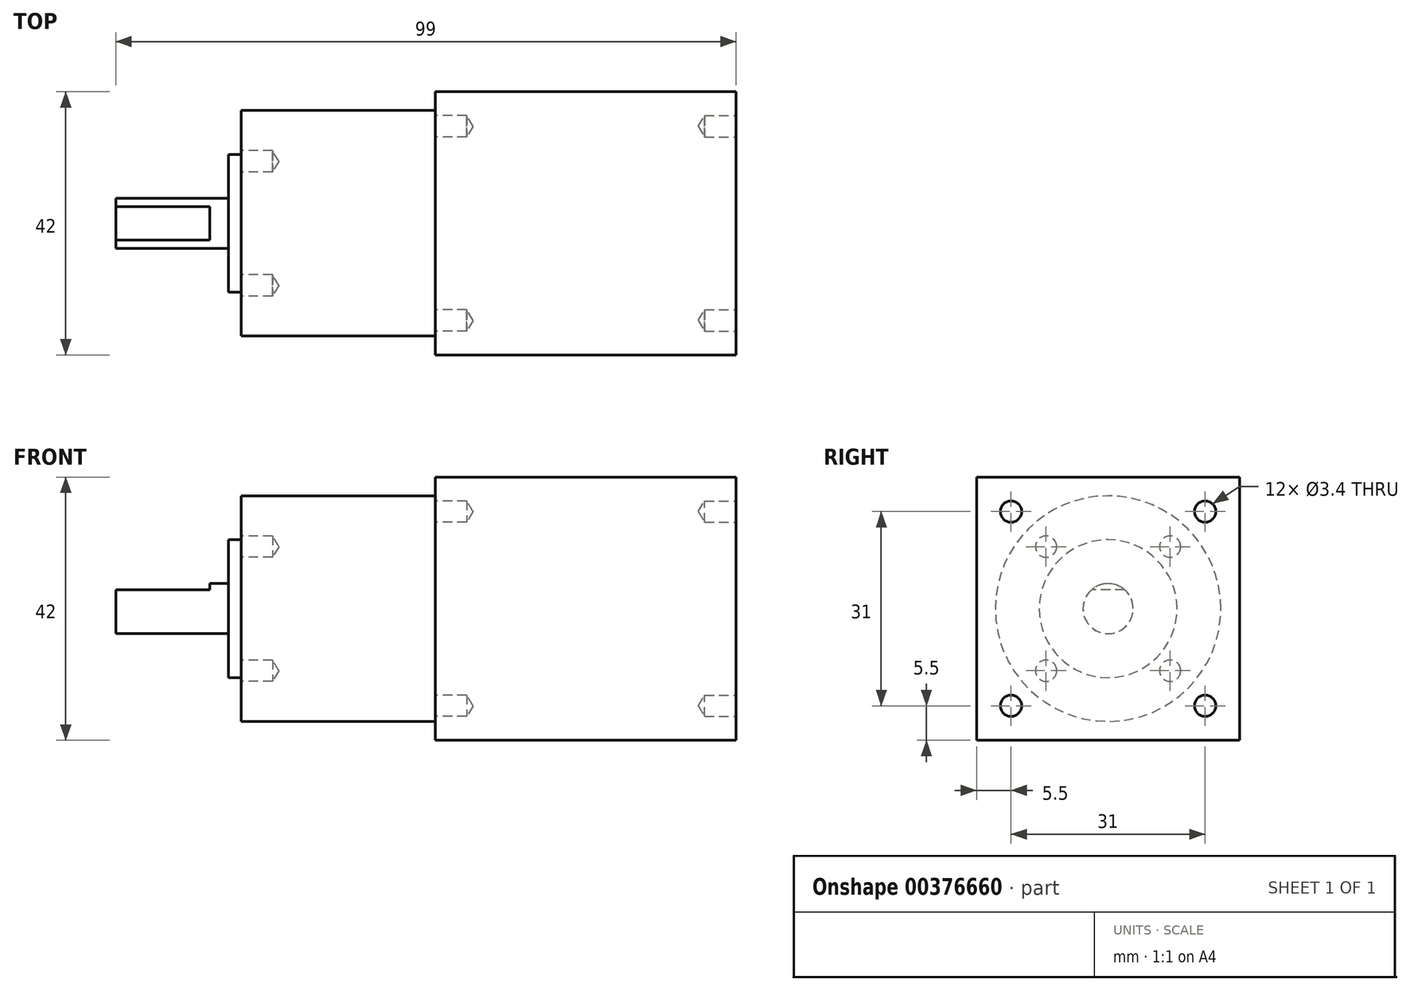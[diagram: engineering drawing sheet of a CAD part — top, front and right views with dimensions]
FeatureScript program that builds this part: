
annotation { "Feature Type Name" : "Feature", "Feature Type Description" : "" }
export const myFeature = defineFeature(function(context is Context, id is Id, definition is map)
    precondition{}
    {
        {
            var Q0;
            Q0=qCreatedBy(makeId("Front.planeOp"),FACE);
            var sketch = newSketch(context, id + "F0", { "sketchPlane" : qUnion([Q0])});
            skLineSegment(sketch, "E0.bottom", {"start": v(0, 21) * mm, "end": v(48, 21) * mm});
            skLineSegment(sketch, "E0.top", {"start": v(0, -21) * mm, "end": v(48, -21) * mm});
            skLineSegment(sketch, "E0.left", {"start": v(0, 21) * mm, "end": v(0, -21) * mm});
            skLineSegment(sketch, "E0.right", {"start": v(48, 21) * mm, "end": v(48, -21) * mm});
            skLineSegment(sketch, "E1.bottom", {"start": v(0, 18) * mm, "end": v(-31, 18) * mm});
            skLineSegment(sketch, "E1.top", {"start": v(0, -18) * mm, "end": v(-31, -18) * mm});
            skLineSegment(sketch, "E1.left", {"start": v(0, 18) * mm, "end": v(0, -18) * mm});
            skLineSegment(sketch, "E1.right", {"start": v(-31, 18) * mm, "end": v(-31, -18) * mm});
            skPoint(sketch, "E2", {"position": v(0, 0) * mm});
            skLineSegment(sketch, "E3.bottom", {"start": v(-31, 11) * mm, "end": v(-33, 11) * mm});
            skLineSegment(sketch, "E3.top", {"start": v(-31, -11) * mm, "end": v(-33, -11) * mm});
            skLineSegment(sketch, "E3.left", {"start": v(-31, 11) * mm, "end": v(-31, -11) * mm});
            skLineSegment(sketch, "E3.right", {"start": v(-33, 11) * mm, "end": v(-33, -11) * mm});
            skPoint(sketch, "E4", {"position": v(-31, 0) * mm});
            skLineSegment(sketch, "E5.bottom", {"start": v(-33, 4) * mm, "end": v(-51, 4) * mm});
            skLineSegment(sketch, "E5.top", {"start": v(-33, -4) * mm, "end": v(-51, -4) * mm});
            skLineSegment(sketch, "E5.left", {"start": v(-33, 4) * mm, "end": v(-33, -4) * mm});
            skLineSegment(sketch, "E5.right", {"start": v(-51, 4) * mm, "end": v(-51, -4) * mm});
            skLineSegment(sketch, "E6", {"start": v(48, 0) * mm, "end": v(48, 0) * mm});
            skPoint(sketch, "E7", {"position": v(-33, 0) * mm});
            skLineSegment(sketch, "E8", {"start": v(-54.92, 0) * mm, "end": v(56.46, 0) * mm});
            skSolve(sketch);
        }
        {
            var Q0;
            {var subQ6=sQuery(id+"F0.wireOp",EDGE,"E0.bottom");Q0=makeQuery(id+"F0.imprint","IMPRINT",FACE,{"disambiguationData":[TD([[makeQuery(id+"F0.imprint","IMPRINT",EDGE,{"derivedFrom":subQ6}),-1.0]])]});}
            var Q1;
            {var subQ6=sQuery(id+"F0.wireOp",EDGE,"E0.top");Q1=makeQuery(id+"F0.imprint","IMPRINT",FACE,{"disambiguationData":[TD([[makeQuery(id+"F0.imprint","IMPRINT",EDGE,{"derivedFrom":subQ6}),1.0]])]});}
            extrude(context, id + "F1", {"entities" : qUnion([Q0, Q1]), "endBound" : BoundingType.SYMMETRIC, "depth" : 42 * mm, "offsetDistance" : 25 * mm});
        }
        {
            var Q0;
            {var subQ5=sQuery(id+"F0.wireOp",EDGE,"E1.bottom");Q0=makeQuery(id+"F0.imprint","IMPRINT",FACE,{"disambiguationData":[TD([[makeQuery(id+"F0.imprint","IMPRINT",EDGE,{"derivedFrom":subQ5}),1.0]])]});}
            var Q1;
            Q1=sQuery(id+"F0.wireOp",EDGE,"E6");
            revolve(context, id + "F2", {"surfaceOperationType" : NewSurfaceOperationType.NEW, "entities" : qUnion([Q0]), "axis" : qUnion([Q1]), "revolveType" : RevolveType.FULL});
        }
        {
            var Q0;
            {var subQ5=sQuery(id+"F0.wireOp",EDGE,"E3.bottom");Q0=makeQuery(id+"F0.imprint","IMPRINT",FACE,{"disambiguationData":[TD([[makeQuery(id+"F0.imprint","IMPRINT",EDGE,{"derivedFrom":subQ5}),1.0]])]});}
            var Q1;
            Q1=sQuery(id+"F0.wireOp",EDGE,"E6");
            revolve(context, id + "F3", {"surfaceOperationType" : NewSurfaceOperationType.NEW, "entities" : qUnion([Q0]), "axis" : qUnion([Q1]), "revolveType" : RevolveType.FULL});
        }
        {
            var Q0;
            {var subQ0=sQuery(id+"F0.wireOp",EDGE,"E5.bottom");Q0=makeQuery(id+"F0.imprint","IMPRINT",FACE,{"disambiguationData":[TD([[makeQuery(id+"F0.imprint","IMPRINT",EDGE,{"derivedFrom":subQ0}),1.0]])]});}
            var Q1;
            Q1=sQuery(id+"F0.wireOp",EDGE,"E6");
            revolve(context, id + "F4", {"surfaceOperationType" : NewSurfaceOperationType.NEW, "entities" : qUnion([Q0]), "axis" : qUnion([Q1]), "revolveType" : RevolveType.FULL});
        }
        {
            var Q0;
            Q0=makeQuery(id+"F4.opRevolve","SWEPT_FACE",FACE,{"disambiguationData":[OSD([sQuery(id+"F0.wireOp",EDGE,"E5.right")])]});
            var sketch = newSketch(context, id + "F5", { "sketchPlane" : qUnion([Q0])});
            skLineSegment(sketch, "E9", {"start": v(-2.65, 3) * mm, "end": v(2.65, 3) * mm});
            skArc(sketch, "E10.0.0", {"start": v(2.65, 3) * mm, "mid": v(0, 4) * mm, "end": v(-2.65, 3) * mm});
            skSolve(sketch);
        }
        {
            var Q0;
            Q0=makeQuery(id+"F5.imprint","IMPRINT",FACE,{"disambiguationData":[TD([[makeQuery(id+"F5.imprint","IMPRINT",EDGE,{"derivedFrom":sQuery(id+"F5.wireOp",EDGE,"E9")}),1.0]])]});
            extrude(context, id + "F6", {"entities" : qUnion([Q0]), "operationType" : NewBodyOperationType.REMOVE, "oppositeDirection" : true, "depth" : 15 * mm, "offsetDistance" : 25 * mm});
        }
        {
            var Q0;
            Q0=makeQuery(id+"F1.opExtrude","SWEPT_FACE",FACE,{"disambiguationData":[OSD([sQuery(id+"F0.wireOp",EDGE,"E0.left"),sQuery(id+"F0.wireOp",EDGE,"E1.left")])]});
            var sketch = newSketch(context, id + "F7", { "sketchPlane" : qUnion([Q0])});
            skCircle(sketch, "E11", {"center": v(0, 0) * mm, "radius": 21.92 * mm, "construction": true});
            skLineSegment(sketch, "E12", {"start": v(15.5, -15.5) * mm, "end": v(-15.5, 15.5) * mm, "construction": true});
            skLineSegment(sketch, "E13", {"start": v(-15.5, -15.5) * mm, "end": v(15.5, 15.5) * mm, "construction": true});
            skPoint(sketch, "E14", {"position": v(-15.5, 15.5) * mm});
            skPoint(sketch, "E15", {"position": v(15.5, 15.5) * mm});
            skPoint(sketch, "E16", {"position": v(15.5, -15.5) * mm});
            skPoint(sketch, "E17", {"position": v(-15.5, -15.5) * mm});
            skSolve(sketch);
        }
        {
            var Q0;
            Q0=makeQuery(id+"F1.opExtrude","SWEPT_FACE",FACE,{"disambiguationData":[OSD([sQuery(id+"F0.wireOp",EDGE,"E0.right")])]});
            var sketch = newSketch(context, id + "F8", { "sketchPlane" : qUnion([Q0])});
            skPoint(sketch, "E18.0", {"position": v(15.5, 15.5) * mm});
            skPoint(sketch, "E19.0", {"position": v(-15.5, 15.5) * mm});
            skPoint(sketch, "E20.0", {"position": v(15.5, -15.5) * mm});
            skPoint(sketch, "E21.0", {"position": v(-15.5, -15.5) * mm});
            skSolve(sketch);
        }
        {
            var Q0;
            Q0=makeQuery(id+"F2.opRevolve","SWEPT_FACE",FACE,{"disambiguationData":[OSD([sQuery(id+"F0.wireOp",EDGE,"E1.right"),sQuery(id+"F0.wireOp",EDGE,"E3.left")])]});
            var sketch = newSketch(context, id + "F9", { "sketchPlane" : qUnion([Q0])});
            skCircle(sketch, "E22", {"center": v(0, 0) * mm, "radius": 14 * mm, "construction": true});
            skPoint(sketch, "E23", {"position": v(-9.9, 9.9) * mm});
            skPoint(sketch, "E24", {"position": v(9.9, 9.9) * mm});
            skPoint(sketch, "E25", {"position": v(9.9, -9.9) * mm});
            skPoint(sketch, "E26", {"position": v(-9.9, -9.9) * mm});
            skLineSegment(sketch, "E27.0", {"start": v(15.5, -15.5) * mm, "end": v(-15.5, 15.5) * mm, "construction": true});
            skLineSegment(sketch, "E28.0", {"start": v(-15.5, -15.5) * mm, "end": v(15.5, 15.5) * mm, "construction": true});
            skSolve(sketch);
        }
        {
            var Q0;
            Q0=sQuery(id+"F9.wireOp",VERTEX,"E23");
            var Q1;
            Q1=sQuery(id+"F9.wireOp",VERTEX,"E24");
            var Q2;
            Q2=sQuery(id+"F9.wireOp",VERTEX,"E25");
            var Q3;
            Q3=sQuery(id+"F9.wireOp",VERTEX,"E26");
            var Q4;
            Q4=sQuery(id+"F7.wireOp",VERTEX,"E14");
            var Q5;
            Q5=sQuery(id+"F7.wireOp",VERTEX,"E15");
            var Q6;
            Q6=sQuery(id+"F7.wireOp",VERTEX,"E16");
            var Q7;
            Q7=sQuery(id+"F7.wireOp",VERTEX,"E17");
            var Q8;
            Q8=sQuery(id+"F8.wireOp",VERTEX,"E19.0");
            var Q9;
            Q9=sQuery(id+"F8.wireOp",VERTEX,"E18.0");
            var Q10;
            Q10=sQuery(id+"F8.wireOp",VERTEX,"E20.0");
            var Q11;
            Q11=sQuery(id+"F8.wireOp",VERTEX,"E21.0");
            var Q12;
            Q12=makeQuery(id+"F2.opRevolve","SWEPT_BODY",BODY,{"disambiguationData":[OSD([sQuery(id+"F0.wireOp",EDGE,"E1.bottom"),sQuery(id+"F0.wireOp",EDGE,"E1.left"),sQuery(id+"F0.wireOp",EDGE,"E1.right"),sQuery(id+"F0.wireOp",EDGE,"E3.left"),sQuery(id+"F0.wireOp",EDGE,"E8")])]});
            var Q13;
            Q13=makeQuery(id+"F1.opExtrude","SWEPT_BODY",BODY,{"disambiguationData":[OSD([sQuery(id+"F0.wireOp",EDGE,"E0.bottom"),sQuery(id+"F0.wireOp",EDGE,"E0.top"),sQuery(id+"F0.wireOp",EDGE,"E0.left"),sQuery(id+"F0.wireOp",EDGE,"E0.right"),sQuery(id+"F0.wireOp",EDGE,"E1.left")])]});
            hole(context, id + "F10", {"style" : HoleStyle.SIMPLE, "endStyle" : HoleEndStyle.BLIND, "standardTappedOrClearance" : lookupTablePath({ "fit" : "Normal", "standard" : "ISO", "size" : "M3", "type" : "Clearance" }), "standardBlindInLast" : lookupTablePath({ "fit" : "Normal", "standard" : "ISO", "size" : "M3", "type" : "Clearance" }), "holeDiameter" : 3.4 * mm, "majorDiameter" : 5 * mm, "holeDepth" : 5 * mm, "tappedDepth" : 12 * mm, "tapClearance" : 3, "startFromSketch" : true, "locations" : qUnion([Q0, Q1, Q2, Q3, Q4, Q5, Q6, Q7, Q8, Q9, Q10, Q11]), "scope" : qUnion([Q12, Q13])});
        }
    });
